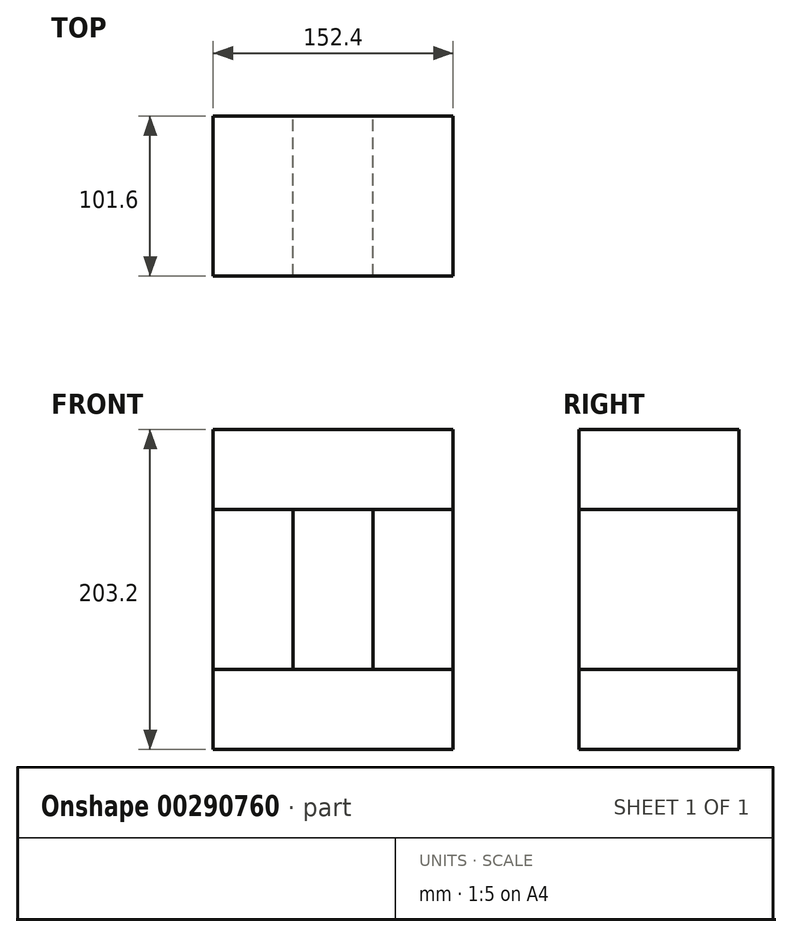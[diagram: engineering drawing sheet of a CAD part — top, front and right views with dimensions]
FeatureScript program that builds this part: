
annotation { "Feature Type Name" : "Feature", "Feature Type Description" : "" }
export const myFeature = defineFeature(function(context is Context, id is Id, definition is map)
    precondition{}
    {
        {
            var Q0;
            Q0=qCreatedBy(makeId("Front.planeOp"),FACE);
            var sketch = newSketch(context, id + "F0", { "sketchPlane" : qUnion([Q0])});
            skLineSegment(sketch, "E0.bottom", {"start": v(-25.4, 50.8) * mm, "end": v(25.4, 50.8) * mm});
            skLineSegment(sketch, "E0.top", {"start": v(-25.4, -50.8) * mm, "end": v(25.4, -50.8) * mm});
            skLineSegment(sketch, "E0.left", {"start": v(-25.4, 50.8) * mm, "end": v(-25.4, -50.8) * mm});
            skLineSegment(sketch, "E0.right", {"start": v(25.4, 50.8) * mm, "end": v(25.4, -50.8) * mm});
            skPoint(sketch, "E0.middle", {"position": v(0, 0) * mm});
            skLineSegment(sketch, "E1.bottom", {"start": v(-25.4, 50.8) * mm, "end": v(-76.2, 50.8) * mm});
            skLineSegment(sketch, "E1.top", {"start": v(-25.4, -50.8) * mm, "end": v(-76.2, -50.8) * mm});
            skLineSegment(sketch, "E1.right", {"start": v(-76.2, 50.8) * mm, "end": v(-76.2, -50.8) * mm});
            skLineSegment(sketch, "E2.bottom", {"start": v(25.4, 50.8) * mm, "end": v(76.2, 50.8) * mm});
            skLineSegment(sketch, "E2.top", {"start": v(25.4, -50.8) * mm, "end": v(76.2, -50.8) * mm});
            skLineSegment(sketch, "E2.right", {"start": v(76.2, 50.8) * mm, "end": v(76.2, -50.8) * mm});
            skLineSegment(sketch, "E3.bottom", {"start": v(-76.2, 50.8) * mm, "end": v(76.2, 50.8) * mm});
            skLineSegment(sketch, "E3.top", {"start": v(-76.2, 101.6) * mm, "end": v(76.2, 101.6) * mm});
            skLineSegment(sketch, "E3.left", {"start": v(-76.2, 50.8) * mm, "end": v(-76.2, 101.6) * mm});
            skLineSegment(sketch, "E3.right", {"start": v(76.2, 50.8) * mm, "end": v(76.2, 101.6) * mm});
            skLineSegment(sketch, "E4.bottom", {"start": v(-76.2, -50.8) * mm, "end": v(76.2, -50.8) * mm});
            skLineSegment(sketch, "E4.top", {"start": v(-76.2, -101.6) * mm, "end": v(76.2, -101.6) * mm});
            skLineSegment(sketch, "E4.left", {"start": v(-76.2, -50.8) * mm, "end": v(-76.2, -101.6) * mm});
            skLineSegment(sketch, "E4.right", {"start": v(76.2, -50.8) * mm, "end": v(76.2, -101.6) * mm});
            skSolve(sketch);
        }
        {
            var Q0;
            {var subQ0=sQuery(id+"F0.wireOp",EDGE,"E0.right");Q0=makeQuery(id+"F0.imprint","IMPRINT",FACE,{"disambiguationData":[TD([[makeQuery(id+"F0.imprint","IMPRINT",EDGE,{"derivedFrom":subQ0}),1.0]])]});}
            var Q1;
            {var subQ0=sQuery(id+"F0.wireOp",EDGE,"E0.left");Q1=makeQuery(id+"F0.imprint","IMPRINT",FACE,{"disambiguationData":[TD([[makeQuery(id+"F0.imprint","IMPRINT",EDGE,{"derivedFrom":subQ0}),-1.0]])]});}
            extrude(context, id + "F1", {"entities" : qUnion([Q0, Q1]), "depth" : 101.6 * mm});
        }
        {
            var Q0;
            Q0=makeQuery(id+"F0.imprint","IMPRINT",FACE,{"disambiguationData":[TD([[makeQuery(id+"F0.imprint","IMPRINT",EDGE,{"derivedFrom":sQuery(id+"F0.wireOp",EDGE,"E3.top")}),-1.0]])]});
            extrude(context, id + "F2", {"entities" : qUnion([Q0]), "depth" : 101.6 * mm});
        }
        {
            var Q0;
            Q0=makeQuery(id+"F0.imprint","IMPRINT",FACE,{"disambiguationData":[TD([[makeQuery(id+"F0.imprint","IMPRINT",EDGE,{"derivedFrom":sQuery(id+"F0.wireOp",EDGE,"E4.top")}),1.0]])]});
            extrude(context, id + "F3", {"entities" : qUnion([Q0]), "depth" : 101.6 * mm});
        }
    });
